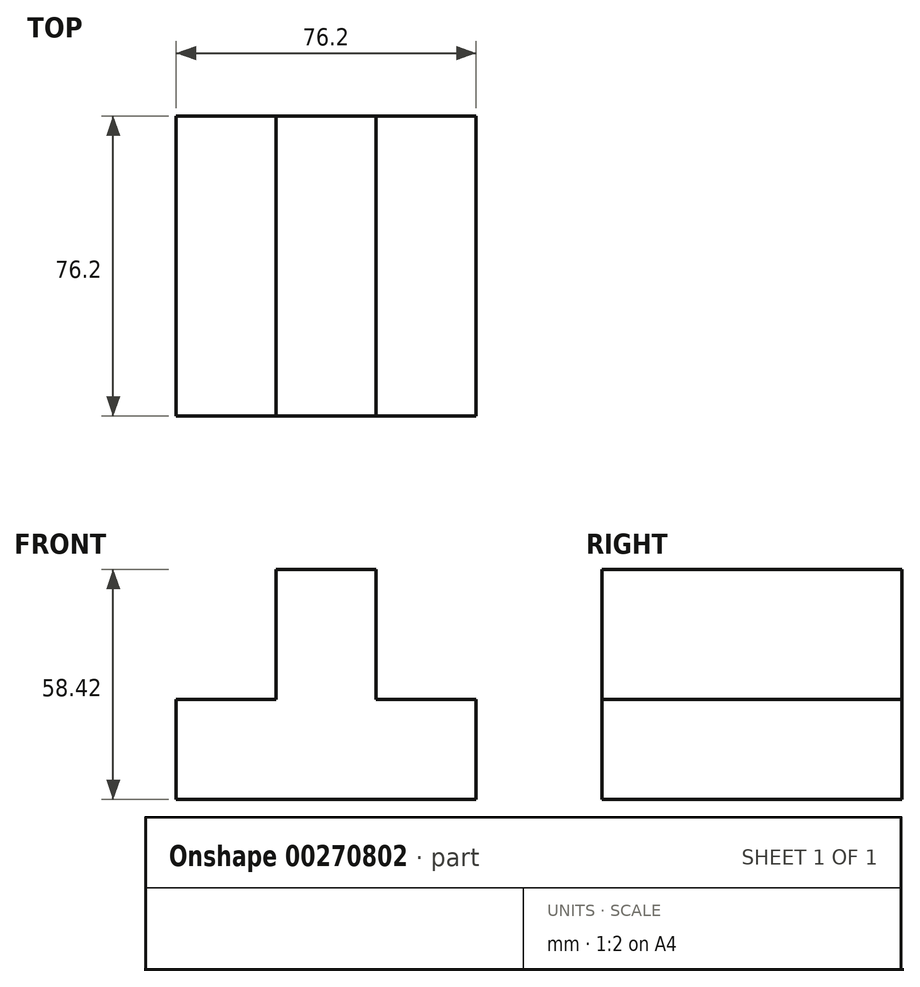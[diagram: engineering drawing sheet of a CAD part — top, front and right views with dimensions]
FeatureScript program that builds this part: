
annotation { "Feature Type Name" : "Feature", "Feature Type Description" : "" }
export const myFeature = defineFeature(function(context is Context, id is Id, definition is map)
    precondition{}
    {
        {
            var Q0;
            Q0=qCreatedBy(makeId("Front.planeOp"),FACE);
            var sketch = newSketch(context, id + "F0", { "sketchPlane" : qUnion([Q0])});
            skLineSegment(sketch, "E0", {"start": v(-57.45, 14.58) * mm, "end": v(-57.45, -10.82) * mm});
            skLineSegment(sketch, "E1", {"start": v(-57.45, -10.82) * mm, "end": v(18.75, -10.82) * mm});
            skLineSegment(sketch, "E2", {"start": v(18.75, -10.82) * mm, "end": v(18.75, 14.58) * mm});
            skLineSegment(sketch, "E3", {"start": v(18.75, 14.58) * mm, "end": v(-6.65, 14.58) * mm});
            skLineSegment(sketch, "E4", {"start": v(-6.65, 14.58) * mm, "end": v(-6.65, 47.6) * mm});
            skLineSegment(sketch, "E5", {"start": v(-6.65, 47.6) * mm, "end": v(-32.05, 47.6) * mm});
            skLineSegment(sketch, "E6", {"start": v(-32.05, 47.6) * mm, "end": v(-32.05, 14.58) * mm});
            skLineSegment(sketch, "E7", {"start": v(-32.05, 14.58) * mm, "end": v(-57.45, 14.58) * mm});
            skSolve(sketch);
        }
        {
            var Q0;
            Q0 = qSketchRegion(id + "F0", true);
            extrude(context, id + "F1", {"entities" : qUnion([Q0]), "depth" : 76.2 * mm});
        }
    });
